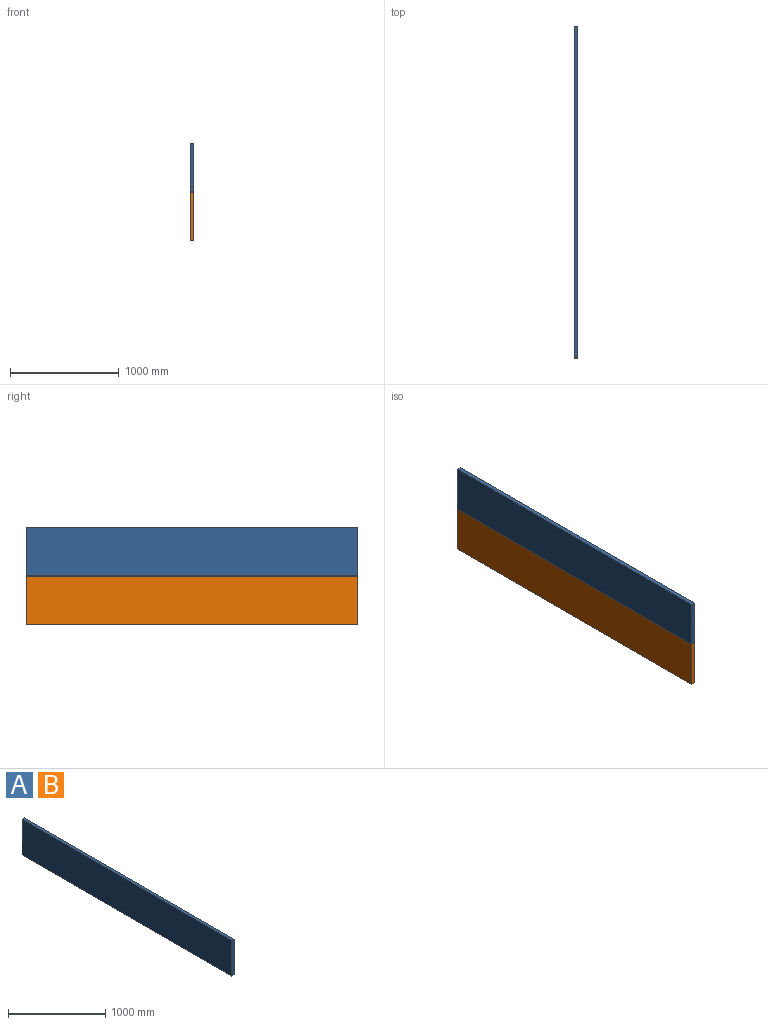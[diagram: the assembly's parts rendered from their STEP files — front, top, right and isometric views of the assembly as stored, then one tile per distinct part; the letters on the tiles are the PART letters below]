
ASSEMBLY  parts=2 mates=1
PART A: 6 faces, bbox 34.5x3048x448.9 mm
  f0: plane 3048x448.87mm, normal (-1,0,0), area 1368143.8mm2, adj f1,f3,f4,f5
  f1: plane 3048x34.49mm, normal (0,0,-1), area 105112.6mm2, adj f0,f2,f4,f5
  f2: plane 3048x448.87mm, normal (1,0,0), area 1368143.8mm2, adj f1,f3,f4,f5
  f3: plane 3048x34.49mm, normal (0,0,1), area 105112.6mm2, adj f0,f2,f4,f5
  f4: plane 448.87x34.49mm, normal (0,-1,0), area 15479.5mm2, adj f0,f1,f2,f3
  f5: plane 448.87x34.49mm, normal (0,1,0), area 15479.5mm2, adj f0,f1,f2,f3
PART B: same geometry as A
PLACE A t=(-938.26,1091.13,-76.12)mm
PLACE B t=(-938.26,1091.13,-524.99)mm
MATE planar B.f3 <-> A.f1  axis (0,0,1) through (-921.02,-432.87,-76.12)mm
